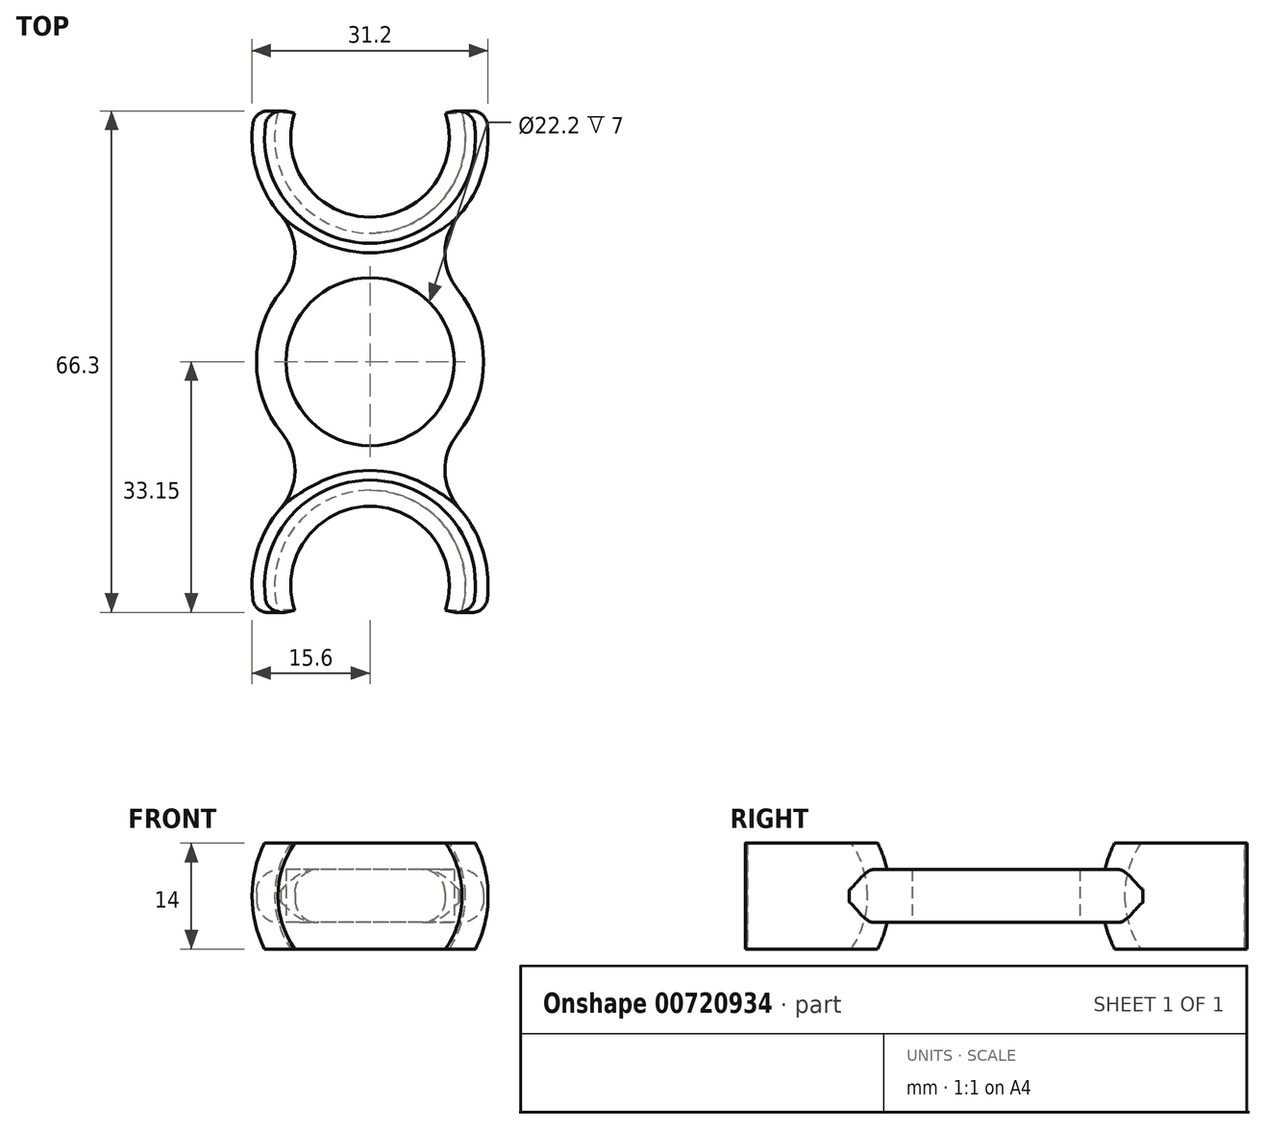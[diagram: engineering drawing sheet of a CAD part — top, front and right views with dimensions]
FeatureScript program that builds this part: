
annotation { "Feature Type Name" : "Feature", "Feature Type Description" : "" }
export const myFeature = defineFeature(function(context is Context, id is Id, definition is map)
    precondition{}
    {
        {
            var Q0;
            Q0=qCreatedBy(makeId("Top.planeOp"),FACE);
            var sketch = newSketch(context, id + "F0", { "sketchPlane" : qUnion([Q0])});
            skArc(sketch, "E0", {"start": v(12.17, -32.86) * mm, "mid": v(0, -17) * mm, "end": v(-12.17, -32.86) * mm});
            skLineSegment(sketch, "E1", {"start": v(0, -17) * mm, "end": v(0, 17) * mm, "construction": true});
            skPoint(sketch, "E2", {"position": v(0, -17) * mm});
            skCircle(sketch, "E3", {"center": v(0, 0) * mm, "radius": 11.1 * mm});
            skLineSegment(sketch, "E4", {"start": v(-12.17, -32.86) * mm, "end": v(0, -29.6) * mm, "construction": true});
            skLineSegment(sketch, "E5", {"start": v(12.17, -32.86) * mm, "end": v(0, -29.6) * mm, "construction": true});
            skArc(sketch, "E6", {"start": v(-11.64, -9.46) * mm, "mid": v(-15, 0) * mm, "end": v(-11.64, 9.46) * mm});
            skArc(sketch, "E7", {"start": v(-11.64, -9.46) * mm, "mid": v(-9.9, -14.45) * mm, "end": v(-11.8, -19.39) * mm});
            skLineSegment(sketch, "E8", {"start": v(-15.07, -33.64) * mm, "end": v(-12.17, -32.86) * mm});
            skLineSegment(sketch, "E9", {"start": v(-11.1, 0) * mm, "end": v(11.1, 0) * mm, "construction": true});
            skArc(sketch, "E10.MirrorCS", {"start": v(-11.64, 9.46) * mm, "mid": v(-9.9, 14.45) * mm, "end": v(-11.8, 19.39) * mm});
            skArc(sketch, "E11.MirrorCS", {"start": v(12.17, 32.86) * mm, "mid": v(0, 17) * mm, "end": v(-12.17, 32.86) * mm});
            skLineSegment(sketch, "E12", {"start": v(-15.07, 33.64) * mm, "end": v(-12.17, 32.86) * mm});
            skLineSegment(sketch, "E13.MirrorCS", {"start": v(15.07, 33.64) * mm, "end": v(12.17, 32.86) * mm});
            skLineSegment(sketch, "E14.MirrorCS", {"start": v(15.07, -33.64) * mm, "end": v(12.17, -32.86) * mm});
            skArc(sketch, "E15.MirrorCS", {"start": v(11.64, -9.46) * mm, "mid": v(9.9, -14.45) * mm, "end": v(11.8, -19.39) * mm});
            skArc(sketch, "E16.MirrorCS", {"start": v(11.64, -9.46) * mm, "mid": v(15, 0) * mm, "end": v(11.64, 9.46) * mm});
            skArc(sketch, "E17.MirrorCS", {"start": v(11.64, 9.46) * mm, "mid": v(9.9, 14.45) * mm, "end": v(11.8, 19.39) * mm});
            skPoint(sketch, "E18.startSnap0", {"position": v(-9.9, -14.45) * mm});
            skArc(sketch, "E19", {"start": v(-15.07, -33.64) * mm, "mid": v(0, -14) * mm, "end": v(15.07, -33.64) * mm});
            skArc(sketch, "E20.MirrorCS", {"start": v(-15.07, 33.64) * mm, "mid": v(0, 14) * mm, "end": v(15.07, 33.64) * mm});
            skPoint(sketch, "E21", {"position": v(-11.8, -19.39) * mm});
            skLineSegment(sketch, "E22", {"start": v(-11.64, -9.46) * mm, "end": v(-17.63, -14.33) * mm, "construction": true});
            skLineSegment(sketch, "E23", {"start": v(-11.8, -19.39) * mm, "end": v(-17.63, -14.33) * mm, "construction": true});
            skLineSegment(sketch, "E24", {"start": v(0, -17) * mm, "end": v(0, -14) * mm});
            skLineSegment(sketch, "E25", {"start": v(0, 14) * mm, "end": v(0, 17) * mm});
            skArc(sketch, "E26", {"start": v(-11.8, -19.39) * mm, "mid": v(0, -16.92) * mm, "end": v(11.8, -19.39) * mm});
            skArc(sketch, "E27.MirrorCS", {"start": v(-11.8, 19.39) * mm, "mid": v(0, 16.92) * mm, "end": v(11.8, 19.39) * mm});
            skArc(sketch, "E28", {"start": v(15.07, -33.64) * mm, "mid": v(0, -45.2) * mm, "end": v(-15.07, -33.64) * mm});
            skArc(sketch, "E29.MirrorCS", {"start": v(15.07, 33.64) * mm, "mid": v(0, 45.2) * mm, "end": v(-15.07, 33.64) * mm});
            skSolve(sketch);
        }
        {
            var Q0;
            Q0=makeQuery(id+"F0.imprint","IMPRINT",FACE,{"disambiguationData":[TD([[makeQuery(id+"F0.imprint","IMPRINT",EDGE,{"derivedFrom":sQuery(id+"F0.wireOp",EDGE,"E3")}),-1.0]])]});
            var Q1;
            {var subQ1=sQuery(id+"F0.wireOp",EDGE,"E19");var subQ3=sQuery(id+"F0.wireOp",EDGE,"E24");var subQ4=makeQuery(id+"F0.imprint","INTERSECT",VERTEX,{"derivedFrom":[subQ1,subQ3]});Q1=makeQuery(id+"F0.imprint","IMPRINT",FACE,{"disambiguationData":[TD([[makeQuery(id+"F0.imprint","IMPRINT",EDGE,{"disambiguationData":[TD([[subQ4,1.0]])],"derivedFrom":subQ3}),1.0]])]});}
            var Q2;
            {var subQ1=sQuery(id+"F0.wireOp",EDGE,"E19");var subQ3=sQuery(id+"F0.wireOp",EDGE,"E24");var subQ4=makeQuery(id+"F0.imprint","INTERSECT",VERTEX,{"derivedFrom":[subQ1,subQ3]});Q2=makeQuery(id+"F0.imprint","IMPRINT",FACE,{"disambiguationData":[TD([[makeQuery(id+"F0.imprint","IMPRINT",EDGE,{"disambiguationData":[TD([[subQ4,1.0]])],"derivedFrom":subQ3}),-1.0]])]});}
            var Q3;
            {var subQ1=sQuery(id+"F0.wireOp",EDGE,"E20.MirrorCS");var subQ3=sQuery(id+"F0.wireOp",EDGE,"E25");var subQ4=makeQuery(id+"F0.imprint","INTERSECT",VERTEX,{"derivedFrom":[subQ1,subQ3]});Q3=makeQuery(id+"F0.imprint","IMPRINT",FACE,{"disambiguationData":[TD([[makeQuery(id+"F0.imprint","IMPRINT",EDGE,{"disambiguationData":[TD([[subQ4,-1.0]])],"derivedFrom":subQ3}),1.0]])]});}
            var Q4;
            {var subQ1=sQuery(id+"F0.wireOp",EDGE,"E20.MirrorCS");var subQ3=sQuery(id+"F0.wireOp",EDGE,"E25");var subQ4=makeQuery(id+"F0.imprint","INTERSECT",VERTEX,{"derivedFrom":[subQ1,subQ3]});Q4=makeQuery(id+"F0.imprint","IMPRINT",FACE,{"disambiguationData":[TD([[makeQuery(id+"F0.imprint","IMPRINT",EDGE,{"disambiguationData":[TD([[subQ4,-1.0]])],"derivedFrom":subQ3}),-1.0]])]});}
            extrude(context, id + "F1", {"entities" : qUnion([Q0, Q1, Q2, Q3, Q4]), "endBound" : BoundingType.SYMMETRIC, "depth" : 7 * mm});
        }
        {
            var Q0;
            {var subQ1=sQuery(id+"F0.wireOp",EDGE,"E19");var subQ3=sQuery(id+"F0.wireOp",EDGE,"E24");var subQ4=makeQuery(id+"F0.imprint","INTERSECT",VERTEX,{"derivedFrom":[subQ1,subQ3]});Q0=makeQuery(id+"F0.imprint","IMPRINT",FACE,{"disambiguationData":[TD([[makeQuery(id+"F0.imprint","IMPRINT",EDGE,{"disambiguationData":[TD([[subQ4,1.0]])],"derivedFrom":subQ3}),-1.0]])]});}
            var Q1;
            {var subQ6=sQuery(id+"F0.wireOp",EDGE,"E14.MirrorCS");Q1=makeQuery(id+"F0.imprint","IMPRINT",FACE,{"disambiguationData":[TD([[makeQuery(id+"F0.imprint","IMPRINT",EDGE,{"derivedFrom":subQ6}),-1.0]])]});}
            var Q2;
            {var subQ1=sQuery(id+"F0.wireOp",EDGE,"E20.MirrorCS");var subQ3=sQuery(id+"F0.wireOp",EDGE,"E25");var subQ4=makeQuery(id+"F0.imprint","INTERSECT",VERTEX,{"derivedFrom":[subQ1,subQ3]});Q2=makeQuery(id+"F0.imprint","IMPRINT",FACE,{"disambiguationData":[TD([[makeQuery(id+"F0.imprint","IMPRINT",EDGE,{"disambiguationData":[TD([[subQ4,-1.0]])],"derivedFrom":subQ3}),-1.0]])]});}
            var Q3;
            {var subQ5=sQuery(id+"F0.wireOp",EDGE,"E13.MirrorCS");Q3=makeQuery(id+"F0.imprint","IMPRINT",FACE,{"disambiguationData":[TD([[makeQuery(id+"F0.imprint","IMPRINT",EDGE,{"derivedFrom":subQ5}),1.0]])]});}
            var Q4;
            Q4=sQuery(id+"F0.wireOp",EDGE,"E1");
            revolve(context, id + "F2", {"operationType" : NewBodyOperationType.ADD, "entities" : qUnion([Q0, Q1, Q2, Q3]), "axis" : qUnion([Q4]), "revolveType" : RevolveType.FULL});
        }
        {
            var Q0;
            Q0=makeQuery(id+"F1.opExtrude","CAP_EDGE",EDGE,{"disambiguationData":[OSD([sQuery(id+"F0.wireOp",EDGE,"E17.MirrorCS")])],"isStart":false});
            var Q1;
            Q1=makeQuery(id+"F1.opExtrude","CAP_EDGE",EDGE,{"disambiguationData":[OSD([sQuery(id+"F0.wireOp",EDGE,"E17.MirrorCS")])],"isStart":true});
            var Q2;
            Q2=makeQuery(id+"F1.opExtrude","CAP_EDGE",EDGE,{"disambiguationData":[OSD([sQuery(id+"F0.wireOp",EDGE,"E10.MirrorCS")])],"isStart":false});
            var Q3;
            Q3=makeQuery(id+"F1.opExtrude","CAP_EDGE",EDGE,{"disambiguationData":[OSD([sQuery(id+"F0.wireOp",EDGE,"E6")])],"isStart":true});
            fillet(context, id + "F3", {"entities" : qUnion([Q0, Q1, Q2, Q3]), "radius" : 3 * mm, "tangentPropagation" : true, "allowEdgeOverflow" : false});
        }
        {
            var Q0;
            Q0=makeQuery(id+"F0.imprint","IMPRINT",FACE,{"disambiguationData":[TD([[makeQuery(id+"F0.imprint","IMPRINT",EDGE,{"derivedFrom":sQuery(id+"F0.wireOp",EDGE,"E3")}),-1.0]])]});
            var Q1;
            {var subQ1=sQuery(id+"F0.wireOp",EDGE,"E19");var subQ3=sQuery(id+"F0.wireOp",EDGE,"E24");var subQ4=makeQuery(id+"F0.imprint","INTERSECT",VERTEX,{"derivedFrom":[subQ1,subQ3]});Q1=makeQuery(id+"F0.imprint","IMPRINT",FACE,{"disambiguationData":[TD([[makeQuery(id+"F0.imprint","IMPRINT",EDGE,{"disambiguationData":[TD([[subQ4,1.0]])],"derivedFrom":subQ3}),1.0]])]});}
            var Q2;
            {var subQ5=sQuery(id+"F0.wireOp",EDGE,"E8");Q2=makeQuery(id+"F0.imprint","IMPRINT",FACE,{"disambiguationData":[TD([[makeQuery(id+"F0.imprint","IMPRINT",EDGE,{"derivedFrom":subQ5}),1.0]])]});}
            var Q3;
            {var subQ1=sQuery(id+"F0.wireOp",EDGE,"E19");var subQ3=sQuery(id+"F0.wireOp",EDGE,"E24");var subQ4=makeQuery(id+"F0.imprint","INTERSECT",VERTEX,{"derivedFrom":[subQ1,subQ3]});Q3=makeQuery(id+"F0.imprint","IMPRINT",FACE,{"disambiguationData":[TD([[makeQuery(id+"F0.imprint","IMPRINT",EDGE,{"disambiguationData":[TD([[subQ4,1.0]])],"derivedFrom":subQ3}),-1.0]])]});}
            var Q4;
            {var subQ6=sQuery(id+"F0.wireOp",EDGE,"E14.MirrorCS");Q4=makeQuery(id+"F0.imprint","IMPRINT",FACE,{"disambiguationData":[TD([[makeQuery(id+"F0.imprint","IMPRINT",EDGE,{"derivedFrom":subQ6}),-1.0]])]});}
            var Q5;
            {var subQ1=sQuery(id+"F0.wireOp",EDGE,"E20.MirrorCS");var subQ3=sQuery(id+"F0.wireOp",EDGE,"E25");var subQ4=makeQuery(id+"F0.imprint","INTERSECT",VERTEX,{"derivedFrom":[subQ1,subQ3]});Q5=makeQuery(id+"F0.imprint","IMPRINT",FACE,{"disambiguationData":[TD([[makeQuery(id+"F0.imprint","IMPRINT",EDGE,{"disambiguationData":[TD([[subQ4,-1.0]])],"derivedFrom":subQ3}),-1.0]])]});}
            var Q6;
            {var subQ1=sQuery(id+"F0.wireOp",EDGE,"E20.MirrorCS");var subQ3=sQuery(id+"F0.wireOp",EDGE,"E25");var subQ4=makeQuery(id+"F0.imprint","INTERSECT",VERTEX,{"derivedFrom":[subQ1,subQ3]});Q6=makeQuery(id+"F0.imprint","IMPRINT",FACE,{"disambiguationData":[TD([[makeQuery(id+"F0.imprint","IMPRINT",EDGE,{"disambiguationData":[TD([[subQ4,-1.0]])],"derivedFrom":subQ3}),1.0]])]});}
            var Q7;
            {var subQ7=sQuery(id+"F0.wireOp",EDGE,"E12");Q7=makeQuery(id+"F0.imprint","IMPRINT",FACE,{"disambiguationData":[TD([[makeQuery(id+"F0.imprint","IMPRINT",EDGE,{"derivedFrom":subQ7}),-1.0]])]});}
            var Q8;
            {var subQ5=sQuery(id+"F0.wireOp",EDGE,"E13.MirrorCS");Q8=makeQuery(id+"F0.imprint","IMPRINT",FACE,{"disambiguationData":[TD([[makeQuery(id+"F0.imprint","IMPRINT",EDGE,{"derivedFrom":subQ5}),1.0]])]});}
            var Q9;
            {var subQ3=sQuery(id+"F0.wireOp",EDGE,"E4");Q9=makeQuery(id+"F0.imprint","IMPRINT",FACE,{"disambiguationData":[TD([[makeQuery(id+"F0.imprint","IMPRINT",EDGE,{"derivedFrom":subQ3}),1.0]])]});}
            var Q10;
            {var subQ3=sQuery(id+"F0.wireOp",EDGE,"f2bedca8-64c1-4297-a2da-92cf3c0b5d7c0.MirrorCS");Q10=makeQuery(id+"F0.imprint","IMPRINT",FACE,{"disambiguationData":[TD([[makeQuery(id+"F0.imprint","IMPRINT",EDGE,{"derivedFrom":subQ3}),-1.0]])]});}
            var Q11;
            {var subQ3=sQuery(id+"F0.wireOp",EDGE,"E8");Q11=makeQuery(id+"F0.imprint","IMPRINT",FACE,{"disambiguationData":[TD([[makeQuery(id+"F0.imprint","IMPRINT",EDGE,{"derivedFrom":subQ3}),-1.0]])]});}
            var Q12;
            {var subQ1=sQuery(id+"F0.wireOp",EDGE,"E12");Q12=makeQuery(id+"F0.imprint","IMPRINT",FACE,{"disambiguationData":[TD([[makeQuery(id+"F0.imprint","IMPRINT",EDGE,{"derivedFrom":subQ1}),1.0]])]});}
            extrude(context, id + "F4", {"entities" : qUnion([Q0, Q1, Q2, Q3, Q4, Q5, Q6, Q7, Q8, Q9, Q10, Q11, Q12]), "operationType" : NewBodyOperationType.INTERSECT, "endBound" : BoundingType.SYMMETRIC, "depth" : 14 * mm});
        }
        {
            var Q0;
            Q0=makeQuery(id+"F2.opRevolve","SWEPT_EDGE",EDGE,{"disambiguationData":[OSD([sQuery(id+"F0.wireOp",EDGE,"E12"),sQuery(id+"F0.wireOp",EDGE,"E20.MirrorCS")])]});
            var Q1;
            Q1=makeQuery(id+"F2.opRevolve","SWEPT_EDGE",EDGE,{"disambiguationData":[OSD([sQuery(id+"F0.wireOp",EDGE,"E8"),sQuery(id+"F0.wireOp",EDGE,"E19")])]});
            var Q2;
            {var subQ0=sQuery(id+"F0.wireOp",EDGE,"E19");Q2=makeQuery(id+"F4.boolean.opBoolean","INTERSECT",EDGE,{"derivedFrom":[makeQuery(id+"F2.opRevolve","SWEPT_FACE",FACE,{"disambiguationData":[OSD([subQ0])]}),makeQuery(id+"F4.boolean.toolComplement.opBoolean","COPY",FACE,{"derivedFrom":makeQuery(id+"F4.opExtrude","CAP_FACE",FACE,{"disambiguationData":[OSD([sQuery(id+"F0.wireOp",EDGE,"E3"),sQuery(id+"F0.wireOp",EDGE,"E6"),sQuery(id+"F0.wireOp",EDGE,"E7"),sQuery(id+"F0.wireOp",EDGE,"E10.MirrorCS"),sQuery(id+"F0.wireOp",EDGE,"E15.MirrorCS"),sQuery(id+"F0.wireOp",EDGE,"E16.MirrorCS"),sQuery(id+"F0.wireOp",EDGE,"E17.MirrorCS"),subQ0,sQuery(id+"F0.wireOp",EDGE,"E20.MirrorCS"),sQuery(id+"F0.wireOp",EDGE,"E28"),sQuery(id+"F0.wireOp",EDGE,"E29.MirrorCS")])],"isStart":false})})]});}
            var Q3;
            {var subQ0=sQuery(id+"F0.wireOp",EDGE,"E19");Q3=makeQuery(id+"F4.boolean.opBoolean","INTERSECT",EDGE,{"derivedFrom":[makeQuery(id+"F2.opRevolve","SWEPT_FACE",FACE,{"disambiguationData":[OSD([subQ0])]}),makeQuery(id+"F4.boolean.toolComplement.opBoolean","COPY",FACE,{"derivedFrom":makeQuery(id+"F4.opExtrude","CAP_FACE",FACE,{"disambiguationData":[OSD([sQuery(id+"F0.wireOp",EDGE,"E3"),sQuery(id+"F0.wireOp",EDGE,"E6"),sQuery(id+"F0.wireOp",EDGE,"E7"),sQuery(id+"F0.wireOp",EDGE,"E10.MirrorCS"),sQuery(id+"F0.wireOp",EDGE,"E15.MirrorCS"),sQuery(id+"F0.wireOp",EDGE,"E16.MirrorCS"),sQuery(id+"F0.wireOp",EDGE,"E17.MirrorCS"),subQ0,sQuery(id+"F0.wireOp",EDGE,"E20.MirrorCS"),sQuery(id+"F0.wireOp",EDGE,"E28"),sQuery(id+"F0.wireOp",EDGE,"E29.MirrorCS")])],"isStart":true})})]});}
            var Q4;
            {var subQ0=sQuery(id+"F0.wireOp",EDGE,"E20.MirrorCS");Q4=makeQuery(id+"F4.boolean.opBoolean","INTERSECT",EDGE,{"derivedFrom":[makeQuery(id+"F2.opRevolve","SWEPT_FACE",FACE,{"disambiguationData":[OSD([subQ0])]}),makeQuery(id+"F4.boolean.toolComplement.opBoolean","COPY",FACE,{"derivedFrom":makeQuery(id+"F4.opExtrude","CAP_FACE",FACE,{"disambiguationData":[OSD([sQuery(id+"F0.wireOp",EDGE,"E3"),sQuery(id+"F0.wireOp",EDGE,"E6"),sQuery(id+"F0.wireOp",EDGE,"E7"),sQuery(id+"F0.wireOp",EDGE,"E10.MirrorCS"),sQuery(id+"F0.wireOp",EDGE,"E15.MirrorCS"),sQuery(id+"F0.wireOp",EDGE,"E16.MirrorCS"),sQuery(id+"F0.wireOp",EDGE,"E17.MirrorCS"),sQuery(id+"F0.wireOp",EDGE,"E19"),subQ0,sQuery(id+"F0.wireOp",EDGE,"E28"),sQuery(id+"F0.wireOp",EDGE,"E29.MirrorCS")])],"isStart":false})})]});}
            var Q5;
            {var subQ0=sQuery(id+"F0.wireOp",EDGE,"E20.MirrorCS");Q5=makeQuery(id+"F4.boolean.opBoolean","INTERSECT",EDGE,{"derivedFrom":[makeQuery(id+"F2.opRevolve","SWEPT_FACE",FACE,{"disambiguationData":[OSD([subQ0])]}),makeQuery(id+"F4.boolean.toolComplement.opBoolean","COPY",FACE,{"derivedFrom":makeQuery(id+"F4.opExtrude","CAP_FACE",FACE,{"disambiguationData":[OSD([sQuery(id+"F0.wireOp",EDGE,"E3"),sQuery(id+"F0.wireOp",EDGE,"E6"),sQuery(id+"F0.wireOp",EDGE,"E7"),sQuery(id+"F0.wireOp",EDGE,"E10.MirrorCS"),sQuery(id+"F0.wireOp",EDGE,"E15.MirrorCS"),sQuery(id+"F0.wireOp",EDGE,"E16.MirrorCS"),sQuery(id+"F0.wireOp",EDGE,"E17.MirrorCS"),sQuery(id+"F0.wireOp",EDGE,"E19"),subQ0,sQuery(id+"F0.wireOp",EDGE,"E28"),sQuery(id+"F0.wireOp",EDGE,"E29.MirrorCS")])],"isStart":true})})]});}
            fillet(context, id + "F5", {"entities" : qUnion([Q0, Q1, Q2, Q3, Q4, Q5]), "radius" : 2 * mm, "tangentPropagation" : true, "allowEdgeOverflow" : false});
        }
    });
